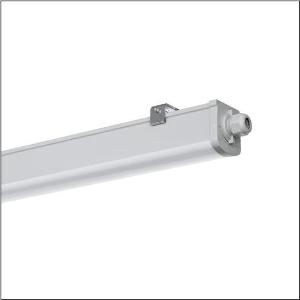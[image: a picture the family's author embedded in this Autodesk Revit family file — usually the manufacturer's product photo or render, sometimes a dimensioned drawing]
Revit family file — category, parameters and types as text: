
# Revit family: monsun_r__31_51fa20dp430b_5f21
name_source: partatom
category: Lighting Fixtures
units: mm (PartAtom-declared; Revit-internal decimal feet)

## family parameters
Cut with Voids When Loaded = No
Host = Face
Light Source = No
Part Type = Normal
Room Calculation Point = No
Round Connector Dimension = Use Diameter
Shared = No

## types (1)
- Monsun® 31 (1 x LED, 3800 lm, 28 W, 4000K)
    Apparent Load = 28 VA
    CIE Flux Codes = 42 72 91 92 100
    Color Rendering = 80
    Color Temperature = 4000K
    Default Elevation = 1800 mm
    Description = Monsun® 31, damp-proof luminaire, primary optical cover: diffuser, of PC, frosted, light emission: direct distribution, primary light characteristic: symmetric, installation type: surface-mounted, LED, rated luminous flux: 3.800lm, luminous efficacy: 136lm/W, light colour: 840, colour temperature: 4000K, control gear: ECG, with terminal, 5+1-pole, max. 2.5mm², through-wiring: 3x 2.5mm² + 3x 1.5mm², mains connection: 220..240V, AC, 50/60Hz, rated input power: 28W, housing, luminaire housing, of PC, light grey (RAL 7035), length: 1.458mm, width: 68mm, height: 76mm, protection rating (complete): IP66, insulation class (complete): insulation class II (safety insulation), certification: CE, ENEC, UKCA, protection symbol: D, impact resistance: IK08, permissible operating ambient temperature: -20..+40°C, corresponds to IFS (International Featured Standards) requirements for safety and quality in the food industry, contact your sales advisor before using the luminaires in applications with unclear chemical exposure, large temperature fluctuations or condensation-forming humidity, packaging unit: 1 piece
    Height = 77 mm
    Lamp = 1 x LED
    Lamp Light Flux = 3800 lm
    Lamp Power = 28 W
    Lamp count = 1
    Length = 1518 mm
    Luminous efficacy = 136 lm/W
    Manufacturer = Siteco
    ModVariant = No
    Model = 51FA20DP430B
    Mounting Place = Ceiling
    Mounting Type = Surface mounted
    Number of Poles = 1
    OnlyDefault = Yes
    Power Factor = 1
    Product Name = Monsun® 31
    Product group = damp-proof luminaire
    ProductGroupID = 301
    Protection Class = Protection class II
    Protection Degree = IP 66
    RLX_Detail_Level = 1
    RLX_Emergency_Light_Flux = 0 lm
    RLX_Emergency_Type = 0
    RLX_Emergency_Type_DB = No
    RlxData = <blob elided: 33129 chars, md5=381b8894>
    Socket = socket
    Standby Power = 0 W
    System Light Flux = 3800 lm
    System Power = 28 W
    Type Comments = Product without accessories
    Type Image = l_1006174.jpg
    URL = http://relux.com
    VarID = ---
    Voltage = 0 V
    Weight = 0.00 kg
    Width = 69 mm

## geometry (parser evidence)
native form markers: Blend x4, Sweep x13
no freeform markers — native parametric forms only
